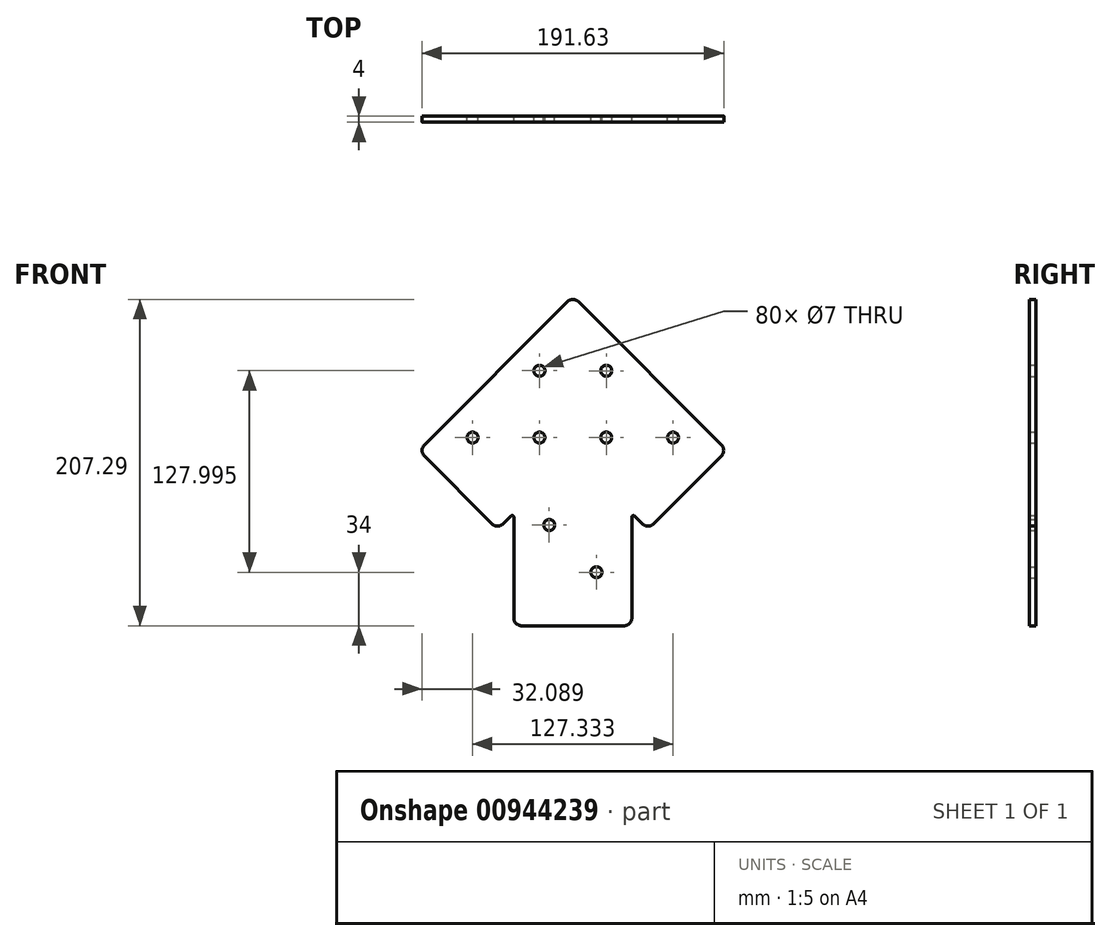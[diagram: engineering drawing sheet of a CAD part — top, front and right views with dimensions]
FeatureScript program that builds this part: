
annotation { "Feature Type Name" : "Feature", "Feature Type Description" : "" }
export const myFeature = defineFeature(function(context is Context, id is Id, definition is map)
    precondition{}
    {
        {
            var Q0;
            Q0=qCreatedBy(makeId("Front.planeOp"),FACE);
            var sketch = newSketch(context, id + "F0", { "sketchPlane" : qUnion([Q0])});
            skCircle(sketch, "E0", {"center": v(-15, -97.99) * mm, "radius": 3.5 * mm});
            skCircle(sketch, "E1", {"center": v(15, -127.99) * mm, "radius": 3.5 * mm});
            skLineSegment(sketch, "E2", {"start": v(-32.5, -161.99) * mm, "end": v(32.5, -161.99) * mm});
            skCircle(sketch, "E3", {"center": v(-21.22, -42.44) * mm, "radius": 3.5 * mm});
            skCircle(sketch, "E4", {"center": v(-63.7, -42.44) * mm, "radius": 3.5 * mm});
            skLineSegment(sketch, "E5", {"start": v(51.24, -97.21) * mm, "end": v(94.37, -54.08) * mm});
            skLineSegment(sketch, "E6", {"start": v(-37.5, -156.99) * mm, "end": v(-37.5, -92.89) * mm});
            skLineSegment(sketch, "E7", {"start": v(-39.2, -92.18) * mm, "end": v(-44.24, -97.21) * mm});
            skPoint(sketch, "E8.visualSharp", {"position": v(-37.5, -90.48) * mm});
            skArc(sketch, "E8.filletArc", {"start": v(-37.5, -92.89) * mm, "mid": v(-38.12, -91.96) * mm, "end": v(-39.2, -92.18) * mm});
            skCircle(sketch, "E9", {"center": v(21.21, -42.43) * mm, "radius": 3.5 * mm});
            skCircle(sketch, "E10", {"center": v(63.63, -42.44) * mm, "radius": 3.5 * mm});
            skCircle(sketch, "E11", {"center": v(-21.22, 0) * mm, "radius": 3.5 * mm});
            skCircle(sketch, "E12", {"center": v(21.22, 0) * mm, "radius": 3.5 * mm});
            skLineSegment(sketch, "E13", {"start": v(44.17, -97.2) * mm, "end": v(39.2, -92.25) * mm});
            skLineSegment(sketch, "E14", {"start": v(3.55, 43.83) * mm, "end": v(94.37, -47) * mm});
            skLineSegment(sketch, "E15", {"start": v(37.5, -92.96) * mm, "end": v(37.5, -156.99) * mm});
            skPoint(sketch, "E16.visualSharp", {"position": v(37.5, -90.54) * mm});
            skArc(sketch, "E16.filletArc", {"start": v(39.2, -92.25) * mm, "mid": v(38.12, -92.03) * mm, "end": v(37.5, -92.96) * mm});
            skPoint(sketch, "E17.visualSharp", {"position": v(-37.5, -161.99) * mm});
            skArc(sketch, "E17.filletArc", {"start": v(-37.5, -156.99) * mm, "mid": v(-36.04, -160.53) * mm, "end": v(-32.5, -161.99) * mm});
            skPoint(sketch, "E18.visualSharp", {"position": v(37.5, -161.99) * mm});
            skArc(sketch, "E18.filletArc", {"start": v(32.5, -161.99) * mm, "mid": v(36.04, -160.53) * mm, "end": v(37.5, -156.99) * mm});
            skPoint(sketch, "E19.visualSharp", {"position": v(47.7, -100.75) * mm});
            skArc(sketch, "E19.filletArc", {"start": v(44.17, -97.2) * mm, "mid": v(47.7, -98.67) * mm, "end": v(51.24, -97.21) * mm});
            skPoint(sketch, "E20.visualSharp", {"position": v(97.9, -50.55) * mm});
            skArc(sketch, "E20.filletArc", {"start": v(94.37, -54.08) * mm, "mid": v(95.84, -50.55) * mm, "end": v(94.37, -47) * mm});
            skPoint(sketch, "E21.visualSharp", {"position": v(-47.78, -100.75) * mm});
            skArc(sketch, "E21.filletArc", {"start": v(-51.31, -97.2) * mm, "mid": v(-47.78, -98.67) * mm, "end": v(-44.24, -97.21) * mm});
            skPoint(sketch, "E22.visualSharp", {"position": v(0, 47.37) * mm});
            skArc(sketch, "E22.filletArc", {"start": v(3.55, 43.83) * mm, "mid": v(0, 45.3) * mm, "end": v(-3.53, 43.83) * mm});
            skLineSegment(sketch, "E23", {"start": v(-94.32, -54.16) * mm, "end": v(-51.31, -97.2) * mm});
            skLineSegment(sketch, "E24", {"start": v(-3.53, 43.83) * mm, "end": v(-94.32, -47.1) * mm});
            skPoint(sketch, "E25.visualSharp", {"position": v(-97.85, -50.63) * mm});
            skArc(sketch, "E25.filletArc", {"start": v(-94.32, -47.1) * mm, "mid": v(-95.79, -50.63) * mm, "end": v(-94.32, -54.16) * mm});
            skSolve(sketch);
        }
        {
            var Q0;
            Q0=makeQuery(id+"F0.imprint","IMPRINT",FACE,{"disambiguationData":[TD([[makeQuery(id+"F0.imprint","IMPRINT",EDGE,{"derivedFrom":sQuery(id+"F0.wireOp",EDGE,"E0")}),-1.0]])]});
            extrude(context, id + "F1", {"entities" : qUnion([Q0]), "depth" : 4 * mm, "offsetDistance" : 25 * mm});
        }
    });
